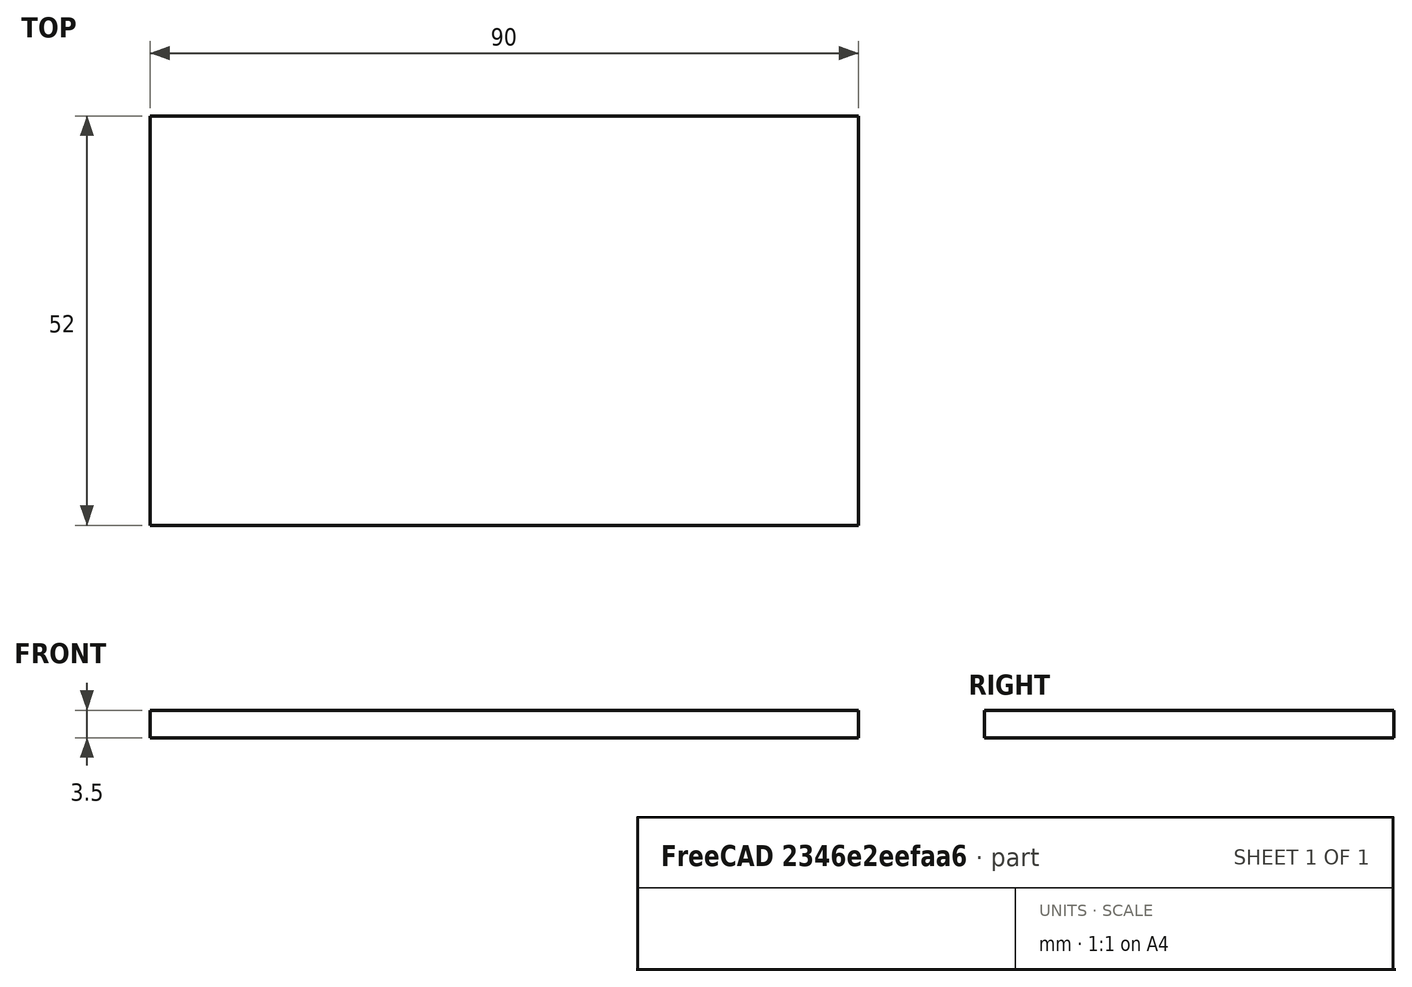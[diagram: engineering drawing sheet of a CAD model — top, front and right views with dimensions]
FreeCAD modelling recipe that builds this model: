
FCSTD DOCUMENT  (FreeCAD 0.18.3R)
Label: letras_liz
License: All rights reserved
LicenseURL: http://en.wikipedia.org/wiki/All_rights_reserved
objects: Path::FeaturePython×3, Part::FeaturePython×2, Part::Part2DObjectPython×1, Part::Extrusion×1, Sketcher::SketchObject×1, PartDesign::Pad×1, PartDesign::Body×1, Part::Cut×1, App::FeaturePython×1, App::DocumentObjectGroup×1, Path::FeatureCompoundPython×1, Mesh::FeaturePython×1
note: 10 computed .brp shape members not serialized (recipe doc carries the construction recipe); baked Part::Feature solids carry a one-line shape summary decoded from their .brp

FEATURE [Part::Part2DObjectPython] ShapeString  # Draft 2D object (typed FeaturePython)
  FontFile = <path>
  Size = 40
  String = Liz
  Tracking = 3
FEATURE [Part::Extrusion] Extrude
  Base = -> ShapeString
  Dir = (0,0,1)
  DirMode = 2
  FaceMakerClass = Part::FaceMakerBullseye
  LengthFwd = 1.5
  LengthRev = 0
  Solid = false
  Symmetric = false
FEATURE [Sketcher::SketchObject] Sketch
  MapMode = 5
  Support = -> [XY_Plane]
  sketch-geometry (4):
    g0: LineSegment StartX=0 StartY=44 StartZ=0 EndX=88 EndY=44 EndZ=0
    g1: LineSegment StartX=88 StartY=44 StartZ=0 EndX=88 EndY=-6 EndZ=0
    g2: LineSegment StartX=88 StartY=-6 StartZ=0 EndX=0 EndY=-6 EndZ=0
    g3: LineSegment StartX=0 StartY=-6 StartZ=0 EndX=0 EndY=44 EndZ=0
  constraints (12):
    c: Coincident(g0,g1)
    c: Coincident(g1,g2)
    c: Coincident(g2,g3)
    c: Coincident(g3,g0)
    c: Horizontal(g0)
    c: Horizontal(g2)
    c: Vertical(g1)
    c: Vertical(g3)
    c: PointOnObject(g2,g-2)
    c: DistanceX(g0,g0) = 88
    c: DistanceY(g3,g3) = 50
    c: DistanceY(g2,g-1) = 6
FEATURE [PartDesign::Pad] Pad
  Length = 1.5
  Length2 = 100
  Profile = -> Sketch
  Refine = true
  Type = 0
FEATURE [PartDesign::Body] Body
  Group = -> [Sketch,Pad]
  Origin = -> Origin
  Tip = -> Pad
FEATURE [Part::Cut] Cut
  Base = -> Body
  Refine = true
  Tool = -> Extrude
FEATURE [App::FeaturePython] SetupSheet  # Path/CAM operation (typed FeaturePython)
  ClearanceHeightExpression = OpStockZMax+SetupSheet.ClearanceHeightOffset
  ClearanceHeightOffset = 15
  FinalDepthExpression = 0
  HorizRapid = 3
  SafeHeightExpression = OpStockZMax+SetupSheet.SafeHeightOffset
  SafeHeightOffset = 5
  StartDepthExpression = 2
  StepDownExpression = 0.5
  VertRapid = 3
FEATURE [Part::FeaturePython] Clone  label="Model-Cut"  # Draft clone (typed FeaturePython)
  AttacherType = Attacher::AttachEngine3D
  Fuse = false
  Objects = -> [Cut]
  PathResource = Model
  Scale = (1,1,1)
FEATURE [App::DocumentObjectGroup] Model
  Group = -> [Clone]
FEATURE [Part::FeaturePython] Stock  # WARN: FeaturePython — macro-defined, semantics opaque (R4)
  Base = -> Model
  ExtXneg = 1
  ExtXpos = 1
  ExtYneg = 1
  ExtYpos = 1
  ExtZneg = 1
  ExtZpos = 1
  Placement = pos=(0,-6,0) rot=(0,0,1;0rad)
  StockType = FromBase
FEATURE [Path::FeaturePython] T2__Fresa_1_8mm  label="T2: Fresa 1.8mm"  # Path/CAM operation (typed FeaturePython)
  HorizFeed = 1
  HorizRapid = 3
  SpindleDir = 0
  SpindleSpeed = 0
  ToolNumber = 2
  VertFeed = 1
  VertRapid = 3
  expr: HorizRapid = 3
  expr: VertRapid = 3
FEATURE [Path::FeaturePython] Pocket_Shape  # Path/CAM operation (typed FeaturePython)
  Active = true
  AreaParams:
    Tolerance = 1e-07
    FitArcs = True
    Simplify = False
    CleanDistance = 0.0
    Accuracy = 0.01
    Unit = 1.0
    MinArcPoints = 4
    MaxArcPoints = 100
    ClipperScale = 10000000.0
    Fill = 0
    Coplanar = 0
    Reorient = True
    Outline = False
    Explode = False
    OpenMode = 0
    Deflection = 0.01
    SubjectFill = 0
    ClipFill = 0
    Offset = 0.0
    ExtraPass = 0
    Stepover = 0.0
    LastStepover = 0.0
    JoinType = 0
    EndType = 0
    MiterLimit = 2.0
    RoundPrecision = 0.0
    PocketMode = 4
    ToolRadius = 0.9
    PocketExtraOffset = 0.0
    PocketStepover = 1.8
    PocketLastStepover = 0.0
    FromCenter = True
    Angle = 45.0
    AngleShift = 0.0
    Shift = 0.0
    Thicken = False
    SectionCount = -1
    Stepdown = 1.0
    SectionOffset = 0.0
    SectionTolerance = 1e-06
    SectionMode = 2
    Project = False
  Base = -> [Clone]
  ClearanceHeight = 17.5
  CutMode = 0
  ExtraOffset = 0
  FinalDepth = 0
  FinishDepth = 0.5
  KeepToolDown = false
  MinTravel = false
  OffsetPattern = 3
  OpFinalDepth = 1.5
  OpStartDepth = 2.5
  OpStockZMax = 2.5
  OpStockZMin = -1
  OpToolDiameter = 1.8
  PathParams = {'orientation': 1, 'feedrate': 1.0, 'feedrate_v': 1.0, 'verbose': True, 'resume_height': 7.5, 'retraction': 17.5, 'return_end': True, 'preamble': False}
  SafeHeight = 7.5
  StartAt = 0
  StartDepth = 1.5
  StartPoint = (0,0,0)
  StepDown = 0.5
  StepOver = 100
  ToolController = -> T2__Fresa_1_8mm
  UseOutline = false
  UseStartPoint = false
  ZigZagAngle = 45
  expr: ClearanceHeight = OpStockZMax + SetupSheet.ClearanceHeightOffset
  expr: SafeHeight = OpStockZMax + SetupSheet.SafeHeightOffset
  expr: StepDown = 0.5
  expr: FinalDepth = 0
  expr: StartDepth = 1.5
FEATURE [Path::FeatureCompoundPython] Operations  # Path/CAM operation (typed FeaturePython)
  Group = -> [Pocket_Shape]
  UsePlacements = false
FEATURE [Path::FeaturePython] Job  # Path/CAM operation (typed FeaturePython)
  GeometryTolerance = 0.01
  Model = -> Model
  Operations = -> Operations
  PostProcessor = 1
  SetupSheet = -> SetupSheet
  Stock = -> Stock
  ToolController = -> [T2__Fresa_1_8mm]
FEATURE [Mesh::FeaturePython] CutMaterial  # WARN: FeaturePython — macro-defined, semantics opaque (R4)
note: 1 file-system path scrubbed to <path> (originals preserved in the JSON sidecar)
